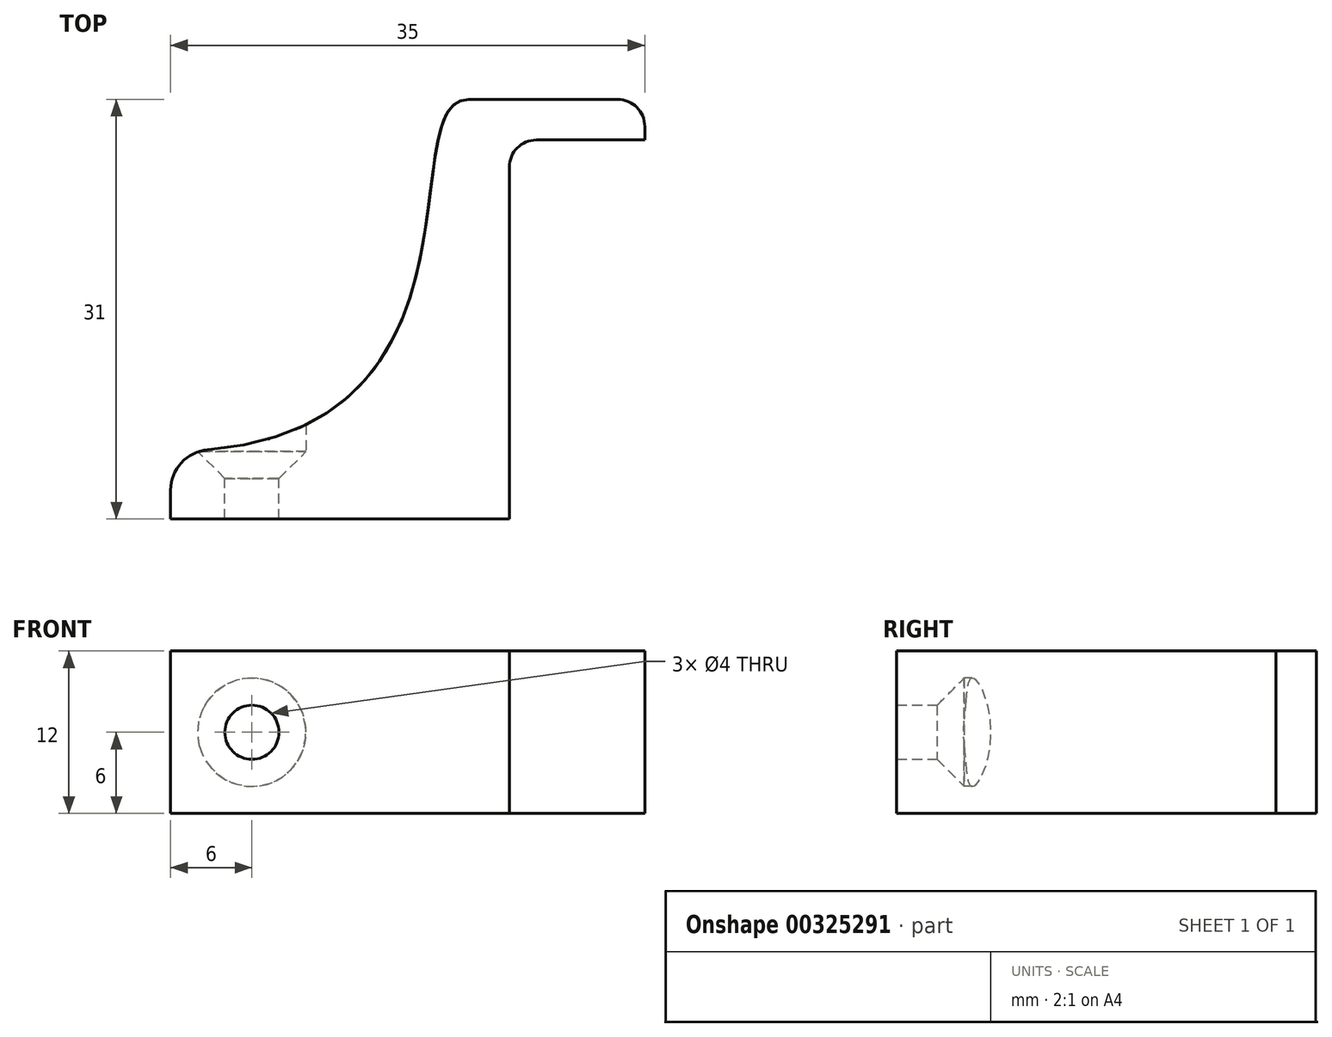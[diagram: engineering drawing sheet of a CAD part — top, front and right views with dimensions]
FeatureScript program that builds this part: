
annotation { "Feature Type Name" : "Feature", "Feature Type Description" : "" }
export const myFeature = defineFeature(function(context is Context, id is Id, definition is map)
    precondition{}
    {
        {
            var Q0;
            Q0=qCreatedBy(makeId("Top.planeOp"),FACE);
            var sketch = newSketch(context, id + "F0", { "sketchPlane" : qUnion([Q0])});
            skLineSegment(sketch, "E0", {"start": v(0, 0) * mm, "end": v(0, 26) * mm});
            skLineSegment(sketch, "E1", {"start": v(2, 28) * mm, "end": v(10, 28) * mm});
            skLineSegment(sketch, "E2", {"start": v(10, 28) * mm, "end": v(10, 29) * mm});
            skLineSegment(sketch, "E3", {"start": v(8, 31) * mm, "end": v(-3, 31) * mm});
            skLineSegment(sketch, "E4", {"start": v(0, 0) * mm, "end": v(-25, 0) * mm});
            skLineSegment(sketch, "E5", {"start": v(-25, 0) * mm, "end": v(-25, 2.12) * mm});
            skFitSpline(sketch, "E6", {"points": [v(-3, 31) * mm, v(-25, 5) * mm], "startDerivative": vector(-18, 0) * mm, "endDerivative": vector(-75, 0) * mm});
            skPoint(sketch, "E7.visualSharp", {"position": v(0, 28) * mm});
            skArc(sketch, "E7.filletArc", {"start": v(2, 28) * mm, "mid": v(0.59, 27.41) * mm, "end": v(0, 26) * mm});
            skPoint(sketch, "E8.visualSharp", {"position": v(10, 31) * mm});
            skArc(sketch, "E8.filletArc", {"start": v(10, 29) * mm, "mid": v(9.41, 30.41) * mm, "end": v(8, 31) * mm});
            skArc(sketch, "E9.filletArc", {"start": v(-22.26, 5.11) * mm, "mid": v(-24.21, 4.15) * mm, "end": v(-25, 2.12) * mm});
            skSolve(sketch);
        }
        {
            var Q0;
            Q0=makeQuery(id+"F0.imprint","IMPRINT",FACE,{"disambiguationData":[TD([[makeQuery(id+"F0.imprint","IMPRINT",EDGE,{"derivedFrom":sQuery(id+"F0.wireOp",EDGE,"E0")}),1.0]])]});
            extrude(context, id + "F1", {"entities" : qUnion([Q0]), "depth" : 12 * mm});
        }
        {
            var Q0;
            Q0=qCreatedBy(makeId("Front.planeOp"),FACE);
            cPlane(context, id + "F2", {"entities" : qUnion([Q0]), "cplaneType" : CPlaneType.OFFSET, "offset" : 5 * mm, "oppositeDirection" : true, "width" : 150 * mm, "height" : 150 * mm});
        }
        {
            var Q0;
            Q0=qCreatedBy(id+"F2.planeOp",FACE);
            var sketch = newSketch(context, id + "F3", { "sketchPlane" : qUnion([Q0])});
            skLineSegment(sketch, "E10", {"start": v(-25, 6) * mm, "end": v(0, 6) * mm, "construction": true});
            skPoint(sketch, "E11", {"position": v(-19, 6) * mm});
            skCircle(sketch, "E12", {"center": v(-19, 6) * mm, "radius": 6 * mm, "construction": true});
            skCircle(sketch, "E13", {"center": v(-19, 6) * mm, "radius": 4 * mm});
            skSolve(sketch);
        }
        {
            var Q0;
            Q0=sQuery(id+"F3.wireOp",VERTEX,"E11");
            var Q1;
            Q1=makeQuery(id+"F1.opExtrude","SWEPT_BODY",BODY,{"disambiguationData":[OSD([sQuery(id+"F0.wireOp",EDGE,"E0"),sQuery(id+"F0.wireOp",EDGE,"E1"),sQuery(id+"F0.wireOp",EDGE,"E2"),sQuery(id+"F0.wireOp",EDGE,"E3"),sQuery(id+"F0.wireOp",EDGE,"E4"),sQuery(id+"F0.wireOp",EDGE,"E5"),sQuery(id+"F0.wireOp",EDGE,"E6"),sQuery(id+"F0.wireOp",EDGE,"E7.filletArc"),sQuery(id+"F0.wireOp",EDGE,"E8.filletArc"),sQuery(id+"F0.wireOp",EDGE,"E9.filletArc")])]});
            hole(context, id + "F4", {"style" : HoleStyle.C_SINK, "endStyle" : HoleEndStyle.BLIND, "oppositeDirection" : true, "holeDiameter" : 4 * mm, "cSinkDiameter" : 8 * mm, "cSinkAngle" : 90 * degree, "holeDepth" : 5 * mm, "tappedDepth" : 12 * mm, "tapClearance" : 3, "startFromSketch" : true, "locations" : qUnion([Q0]), "scope" : qUnion([Q1])});
        }
        {
            var Q0;
            Q0=makeQuery(id+"F3.imprint","IMPRINT",FACE,{"disambiguationData":[TD([[makeQuery(id+"F3.imprint","IMPRINT",EDGE,{"derivedFrom":sQuery(id+"F3.wireOp",EDGE,"E13")}),1.0]])]});
            extrude(context, id + "F5", {"entities" : qUnion([Q0]), "operationType" : NewBodyOperationType.REMOVE, "endBound" : BoundingType.THROUGH_ALL, "oppositeDirection" : true, "depth" : 25 * mm});
        }
    });
